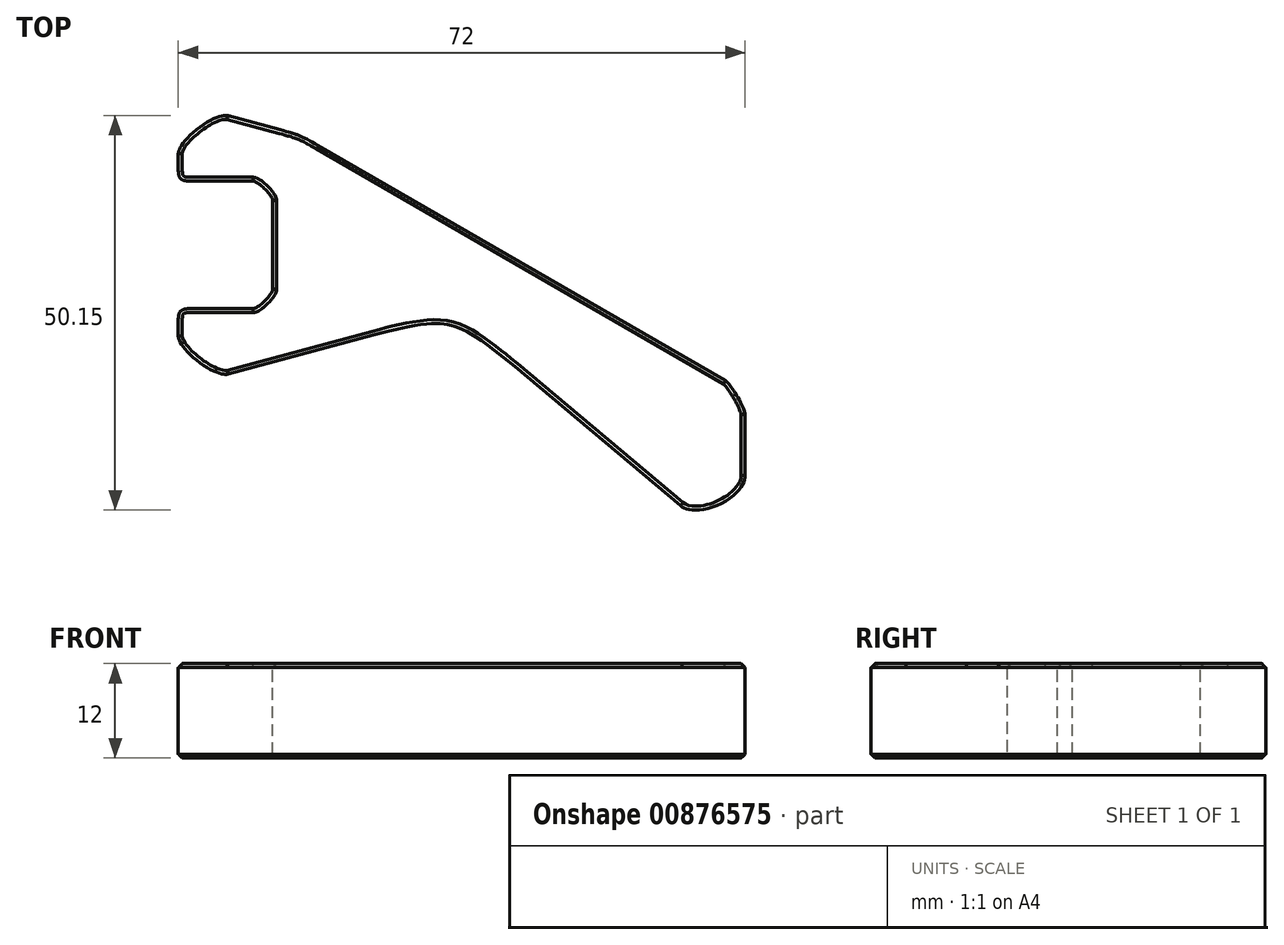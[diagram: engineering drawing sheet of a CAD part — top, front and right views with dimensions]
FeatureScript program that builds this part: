
annotation { "Feature Type Name" : "Feature", "Feature Type Description" : "" }
export const myFeature = defineFeature(function(context is Context, id is Id, definition is map)
    precondition{}
    {
        {
            var Q0;
            Q0=qCreatedBy(makeId("Top.planeOp"),FACE);
            var sketch = newSketch(context, id + "F0", { "sketchPlane" : qUnion([Q0])});
            skLineSegment(sketch, "E0", {"start": v(-12, 0) * mm, "end": v(0, 0) * mm});
            skLineSegment(sketch, "E1", {"start": v(0, 0) * mm, "end": v(0, 16.2) * mm});
            skLineSegment(sketch, "E2", {"start": v(0, 16.2) * mm, "end": v(-12, 16.2) * mm});
            skLineSegment(sketch, "E3", {"start": v(-12, 16.2) * mm, "end": v(-12, 26.2) * mm});
            skLineSegment(sketch, "E4", {"start": v(-12, 26.2) * mm, "end": v(3.45, 22.06) * mm});
            skLineSegment(sketch, "E5", {"start": v(3.45, 22.06) * mm, "end": v(60, -10.59) * mm});
            skLineSegment(sketch, "E6", {"start": v(60, -10.59) * mm, "end": v(60, -31.92) * mm});
            skLineSegment(sketch, "E7", {"start": v(60, -31.92) * mm, "end": v(22.77, -0.68) * mm});
            skLineSegment(sketch, "E8", {"start": v(22.77, -0.68) * mm, "end": v(-12, -10) * mm});
            skLineSegment(sketch, "E9", {"start": v(-12, -10) * mm, "end": v(-12, 0) * mm});
            skSolve(sketch);
        }
        {
            var Q0;
            Q0=makeQuery(id+"F0.imprint","IMPRINT",FACE,{"disambiguationData":[TD([[makeQuery(id+"F0.imprint","IMPRINT",EDGE,{"derivedFrom":sQuery(id+"F0.wireOp",EDGE,"E0")}),-1.0]])]});
            extrude(context, id + "F1", {"entities" : qUnion([Q0]), "endBound" : BoundingType.SYMMETRIC, "depth" : 12 * mm, "offsetDistance" : 25 * mm});
        }
        {
            var Q0;
            Q0=makeQuery(id+"F1.opExtrude","SWEPT_EDGE",EDGE,{"disambiguationData":[OSD([sQuery(id+"F0.wireOp",EDGE,"E1"),sQuery(id+"F0.wireOp",EDGE,"E2")])]});
            var Q1;
            Q1=makeQuery(id+"F1.opExtrude","SWEPT_EDGE",EDGE,{"disambiguationData":[OSD([sQuery(id+"F0.wireOp",EDGE,"E0"),sQuery(id+"F0.wireOp",EDGE,"E1")])]});
            fillet(context, id + "F2", {"entities" : qUnion([Q0, Q1]), "radius" : 2.5 * mm, "tangentPropagation" : true, "rho" : .2, "crossSection" : FilletCrossSection.CONIC, "allowEdgeOverflow" : false});
        }
        {
            var Q0;
            Q0=makeQuery(id+"F1.opExtrude","SWEPT_EDGE",EDGE,{"disambiguationData":[OSD([sQuery(id+"F0.wireOp",EDGE,"E7"),sQuery(id+"F0.wireOp",EDGE,"E8")])]});
            var Q1;
            Q1=makeQuery(id+"F1.opExtrude","SWEPT_EDGE",EDGE,{"disambiguationData":[OSD([sQuery(id+"F0.wireOp",EDGE,"E4"),sQuery(id+"F0.wireOp",EDGE,"E5")])]});
            fillet(context, id + "F3", {"entities" : qUnion([Q0, Q1]), "radius" : 20 * mm, "tangentPropagation" : true, "rho" : .7, "crossSection" : FilletCrossSection.CONIC, "allowEdgeOverflow" : false});
        }
        {
            var Q0;
            Q0=makeQuery(id+"F1.opExtrude","SWEPT_EDGE",EDGE,{"disambiguationData":[OSD([sQuery(id+"F0.wireOp",EDGE,"E2"),sQuery(id+"F0.wireOp",EDGE,"E3")])]});
            var Q1;
            Q1=makeQuery(id+"F1.opExtrude","SWEPT_EDGE",EDGE,{"disambiguationData":[OSD([sQuery(id+"F0.wireOp",EDGE,"E0"),sQuery(id+"F0.wireOp",EDGE,"E9")])]});
            fillet(context, id + "F4", {"entities" : qUnion([Q0, Q1]), "radius" : 1.5 * mm, "tangentPropagation" : true, "rho" : .6, "crossSection" : FilletCrossSection.CONIC, "allowEdgeOverflow" : false});
        }
        {
            var Q0;
            Q0=makeQuery(id+"F1.opExtrude","SWEPT_EDGE",EDGE,{"disambiguationData":[OSD([sQuery(id+"F0.wireOp",EDGE,"E3"),sQuery(id+"F0.wireOp",EDGE,"E4")])]});
            var Q1;
            Q1=makeQuery(id+"F1.opExtrude","SWEPT_EDGE",EDGE,{"disambiguationData":[OSD([sQuery(id+"F0.wireOp",EDGE,"E8"),sQuery(id+"F0.wireOp",EDGE,"E9")])]});
            var Q2;
            Q2=makeQuery(id+"F1.opExtrude","SWEPT_EDGE",EDGE,{"disambiguationData":[OSD([sQuery(id+"F0.wireOp",EDGE,"E6"),sQuery(id+"F0.wireOp",EDGE,"E7")])]});
            var Q3;
            Q3=makeQuery(id+"F1.opExtrude","SWEPT_EDGE",EDGE,{"disambiguationData":[OSD([sQuery(id+"F0.wireOp",EDGE,"E5"),sQuery(id+"F0.wireOp",EDGE,"E6")])]});
            fillet(context, id + "F5", {"entities" : qUnion([Q0, Q1, Q2, Q3]), "radius" : 5 * mm, "tangentPropagation" : true, "rho" : .2, "crossSection" : FilletCrossSection.CONIC, "allowEdgeOverflow" : false});
        }
        {
            var Q0;
            Q0=makeQuery(id+"F1.opExtrude","CAP_FACE",FACE,{"disambiguationData":[OSD([sQuery(id+"F0.wireOp",EDGE,"E0"),sQuery(id+"F0.wireOp",EDGE,"E1"),sQuery(id+"F0.wireOp",EDGE,"E2"),sQuery(id+"F0.wireOp",EDGE,"E3"),sQuery(id+"F0.wireOp",EDGE,"E4"),sQuery(id+"F0.wireOp",EDGE,"E5"),sQuery(id+"F0.wireOp",EDGE,"E6"),sQuery(id+"F0.wireOp",EDGE,"E7"),sQuery(id+"F0.wireOp",EDGE,"E8"),sQuery(id+"F0.wireOp",EDGE,"E9")])],"isStart":false});
            var Q1;
            Q1=makeQuery(id+"F1.opExtrude","CAP_FACE",FACE,{"disambiguationData":[OSD([sQuery(id+"F0.wireOp",EDGE,"E0"),sQuery(id+"F0.wireOp",EDGE,"E1"),sQuery(id+"F0.wireOp",EDGE,"E2"),sQuery(id+"F0.wireOp",EDGE,"E3"),sQuery(id+"F0.wireOp",EDGE,"E4"),sQuery(id+"F0.wireOp",EDGE,"E5"),sQuery(id+"F0.wireOp",EDGE,"E6"),sQuery(id+"F0.wireOp",EDGE,"E7"),sQuery(id+"F0.wireOp",EDGE,"E8"),sQuery(id+"F0.wireOp",EDGE,"E9")])],"isStart":true});
            chamfer(context, id + "F6", {"entities" : qUnion([Q0, Q1]), "width" : .5 * mm, "tangentPropagation" : true});
        }
    });
